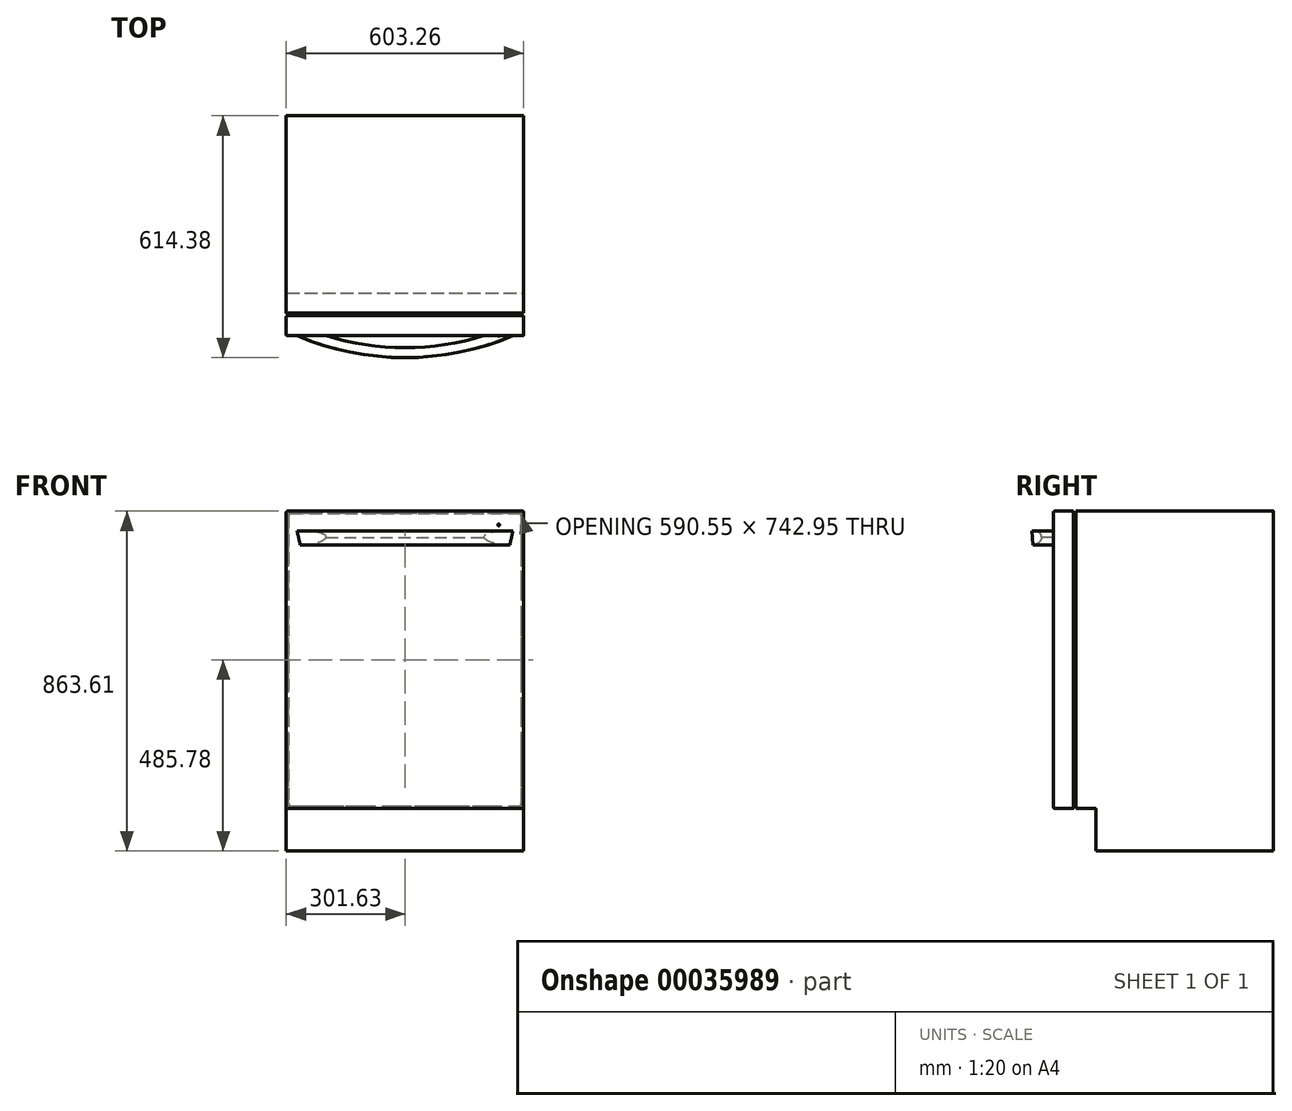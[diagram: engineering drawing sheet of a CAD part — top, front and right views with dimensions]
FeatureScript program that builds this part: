
annotation { "Feature Type Name" : "Feature", "Feature Type Description" : "" }
export const myFeature = defineFeature(function(context is Context, id is Id, definition is map)
    precondition{}
    {
        {
            var Q0;
            Q0=qCreatedBy(makeId("Front.planeOp"),FACE);
            var sketch = newSketch(context, id + "F0", { "sketchPlane" : qUnion([Q0])});
            skLineSegment(sketch, "E0.bottom", {"start": v(-301.63, 377.83) * mm, "end": v(301.63, 377.83) * mm});
            skLineSegment(sketch, "E0.top", {"start": v(-301.63, -377.82) * mm, "end": v(301.63, -377.82) * mm});
            skLineSegment(sketch, "E0.left", {"start": v(-301.63, 377.83) * mm, "end": v(-301.63, -377.82) * mm});
            skLineSegment(sketch, "E0.right", {"start": v(301.63, 377.83) * mm, "end": v(301.63, -377.82) * mm});
            skLineSegment(sketch, "E1", {"start": v(-301.63, -377.83) * mm, "end": v(301.63, 377.83) * mm, "construction": true});
            skPoint(sketch, "E2", {"position": v(0, 0) * mm});
            skSolve(sketch);
        }
        {
            var Q0;
            Q0=makeQuery(id+"F0.imprint","IMPRINT",FACE,{"disambiguationData":[TD([[makeQuery(id+"F0.imprint","IMPRINT",EDGE,{"derivedFrom":sQuery(id+"F0.wireOp",EDGE,"E0.bottom")}),-1.0]])]});
            extrude(context, id + "F1", {"entities" : qUnion([Q0]), "depth" : 50.8 * mm});
        }
        {
            var Q0;
            Q0=makeQuery(id+"F1.opExtrude","CAP_FACE",FACE,{"disambiguationData":[OSD([sQuery(id+"F0.wireOp",EDGE,"E0.bottom"),sQuery(id+"F0.wireOp",EDGE,"E0.top"),sQuery(id+"F0.wireOp",EDGE,"E0.left"),sQuery(id+"F0.wireOp",EDGE,"E0.right")])],"isStart":true});
            var sketch = newSketch(context, id + "F2", { "sketchPlane" : qUnion([Q0])});
            skLineSegment(sketch, "E3.0", {"start": v(295.28, 371.48) * mm, "end": v(295.28, -371.47) * mm});
            skLineSegment(sketch, "E3.1", {"start": v(295.28, 371.48) * mm, "end": v(-295.28, 371.48) * mm});
            skLineSegment(sketch, "E3.2", {"start": v(-295.28, 371.48) * mm, "end": v(-295.28, -371.47) * mm});
            skLineSegment(sketch, "E3.3", {"start": v(295.28, -371.47) * mm, "end": v(-295.28, -371.47) * mm});
            skSolve(sketch);
        }
        {
            var Q0;
            Q0=makeQuery(id+"F2.imprint","IMPRINT",FACE,{"disambiguationData":[TD([[makeQuery(id+"F2.imprint","IMPRINT",EDGE,{"derivedFrom":sQuery(id+"F2.wireOp",EDGE,"E3.0")}),-1.0]])]});
            extrude(context, id + "F3", {"entities" : qUnion([Q0]), "operationType" : NewBodyOperationType.ADD, "depth" : 6.35 * mm});
        }
        {
            var Q0;
            Q0=makeQuery(id+"F3.opExtrude","CAP_FACE",FACE,{"disambiguationData":[OSD([sQuery(id+"F2.wireOp",EDGE,"E3.0"),sQuery(id+"F2.wireOp",EDGE,"E3.1"),sQuery(id+"F2.wireOp",EDGE,"E3.2"),sQuery(id+"F2.wireOp",EDGE,"E3.3")])],"isStart":false});
            var sketch = newSketch(context, id + "F4", { "sketchPlane" : qUnion([Q0])});
            skLineSegment(sketch, "E4.bottom", {"start": v(301.63, 377.83) * mm, "end": v(-301.63, 377.82) * mm});
            skLineSegment(sketch, "E4.top", {"start": v(301.63, -485.77) * mm, "end": v(-301.62, -485.77) * mm});
            skLineSegment(sketch, "E4.left", {"start": v(301.63, 377.83) * mm, "end": v(301.63, -485.77) * mm});
            skLineSegment(sketch, "E4.right", {"start": v(-301.63, 377.82) * mm, "end": v(-301.62, -485.77) * mm});
            skSolve(sketch);
        }
        {
            var Q0;
            Q0=makeQuery(id+"F4.imprint","IMPRINT",FACE,{"disambiguationData":[TD([[makeQuery(id+"F4.imprint","IMPRINT",EDGE,{"derivedFrom":makeQuery(id+"F3.opExtrude","CAP_EDGE",EDGE,{"disambiguationData":[OSD([sQuery(id+"F2.wireOp",EDGE,"E3.0")])],"isStart":false})}),-1.0]])]});
            var Q1;
            Q1=makeQuery(id+"F4.imprint","IMPRINT",FACE,{"disambiguationData":[TD([[makeQuery(id+"F4.imprint","IMPRINT",EDGE,{"derivedFrom":sQuery(id+"F4.wireOp",EDGE,"E4.bottom")}),1.0]])]});
            extrude(context, id + "F5", {"entities" : qUnion([Q0, Q1]), "operationType" : NewBodyOperationType.ADD, "depth" : 501.65 * mm});
        }
        {
            var Q0;
            Q0=makeQuery(id+"F5.opExtrude","SWEPT_FACE",FACE,{"disambiguationData":[OSD([sQuery(id+"F4.wireOp",EDGE,"E4.right")])]});
            var sketch = newSketch(context, id + "F6", { "sketchPlane" : qUnion([Q0])});
            skLineSegment(sketch, "E5.bottom", {"start": v(-50.8, -377.82) * mm, "end": v(57.15, -377.82) * mm});
            skLineSegment(sketch, "E5.top", {"start": v(-50.8, -485.77) * mm, "end": v(57.15, -485.77) * mm});
            skLineSegment(sketch, "E5.left", {"start": v(-50.8, -377.82) * mm, "end": v(-50.8, -485.77) * mm});
            skLineSegment(sketch, "E5.right", {"start": v(57.15, -377.82) * mm, "end": v(57.15, -485.77) * mm});
            skSolve(sketch);
        }
        {
            var Q0;
            {var subQ6=sQuery(id+"F6.wireOp",EDGE,"E5.right");Q0=makeQuery(id+"F6.imprint","IMPRINT",FACE,{"disambiguationData":[TD([[makeQuery(id+"F6.imprint","IMPRINT",EDGE,{"derivedFrom":subQ6}),-1.0]])]});}
            extrude(context, id + "F7", {"entities" : qUnion([Q0]), "operationType" : NewBodyOperationType.REMOVE, "endBound" : BoundingType.THROUGH_ALL, "oppositeDirection" : true, "depth" : 25.4 * mm});
        }
        {
            var Q0;
            Q0=makeQuery(id+"F5.opExtrude","SWEPT_EDGE",EDGE,{"disambiguationData":[OSD([sQuery(id+"F4.wireOp",EDGE,"E4.bottom"),sQuery(id+"F4.wireOp",EDGE,"E4.right")])]});
            var Q1;
            Q1=makeQuery(id+"F1.opExtrude","SWEPT_EDGE",EDGE,{"disambiguationData":[OSD([sQuery(id+"F0.wireOp",EDGE,"E0.bottom"),sQuery(id+"F0.wireOp",EDGE,"E0.right")])]});
            var Q2;
            Q2=makeQuery(id+"F5.opExtrude","SWEPT_EDGE",EDGE,{"disambiguationData":[OSD([sQuery(id+"F4.wireOp",EDGE,"E4.bottom"),sQuery(id+"F4.wireOp",EDGE,"E4.left")])]});
            var Q3;
            Q3=makeQuery(id+"F1.opExtrude","SWEPT_FACE",FACE,{"disambiguationData":[OSD([sQuery(id+"F0.wireOp",EDGE,"E0.bottom")])]});
            var Q4;
            Q4=makeQuery(id+"F1.opExtrude","CAP_FACE",FACE,{"disambiguationData":[OSD([sQuery(id+"F0.wireOp",EDGE,"E0.bottom"),sQuery(id+"F0.wireOp",EDGE,"E0.top"),sQuery(id+"F0.wireOp",EDGE,"E0.left"),sQuery(id+"F0.wireOp",EDGE,"E0.right")])],"isStart":false});
            var Q5;
            Q5=makeQuery(id+"F1.opExtrude","SWEPT_FACE",FACE,{"disambiguationData":[OSD([sQuery(id+"F0.wireOp",EDGE,"E0.left")])]});
            var Q6;
            Q6=makeQuery(id+"F1.opExtrude","SWEPT_FACE",FACE,{"disambiguationData":[OSD([sQuery(id+"F0.wireOp",EDGE,"E0.top")])]});
            var Q7;
            Q7=makeQuery(id+"F1.opExtrude","SWEPT_FACE",FACE,{"disambiguationData":[OSD([sQuery(id+"F0.wireOp",EDGE,"E0.right")])]});
            var Q8;
            Q8=makeQuery(id+"F7.boolean.opBoolean","COPY",EDGE,{"derivedFrom":makeQuery(id+"F7.opExtrude","CAP_EDGE",EDGE,{"disambiguationData":[OSD([sQuery(id+"F6.wireOp",EDGE,"E5.bottom")])],"isStart":true})});
            var Q9;
            Q9=makeQuery(id+"F7.boolean.opBoolean","INTERSECT",EDGE,{"derivedFrom":[makeQuery(id+"F5.opExtrude","SWEPT_FACE",FACE,{"disambiguationData":[OSD([sQuery(id+"F4.wireOp",EDGE,"E4.left")])]}),makeQuery(id+"F7.opExtrude","SWEPT_FACE",FACE,{"disambiguationData":[OSD([sQuery(id+"F6.wireOp",EDGE,"E5.bottom")])]})]});
            fillet(context, id + "F8", {"entities" : qUnion([Q0, Q1, Q2, Q3, Q4, Q5, Q6, Q7, Q8, Q9]), "radius" : 3.17 * mm, "tangentPropagation" : true, "rho" : 0.5, "crossSection" : FilletCrossSection.CONIC, "allowEdgeOverflow" : false});
        }
        {
            var Q0;
            Q0=makeQuery(id+"F3.opExtrude","SWEPT_EDGE",EDGE,{"disambiguationData":[OSD([sQuery(id+"F2.wireOp",EDGE,"E3.1"),sQuery(id+"F2.wireOp",EDGE,"E3.2")])]});
            var Q1;
            Q1=makeQuery(id+"F3.opExtrude","SWEPT_EDGE",EDGE,{"disambiguationData":[OSD([sQuery(id+"F2.wireOp",EDGE,"E3.0"),sQuery(id+"F2.wireOp",EDGE,"E3.1")])]});
            var Q2;
            Q2=makeQuery(id+"F3.opExtrude","SWEPT_EDGE",EDGE,{"disambiguationData":[OSD([sQuery(id+"F2.wireOp",EDGE,"E3.0"),sQuery(id+"F2.wireOp",EDGE,"E3.3")])]});
            var Q3;
            Q3=makeQuery(id+"F3.opExtrude","SWEPT_EDGE",EDGE,{"disambiguationData":[OSD([sQuery(id+"F2.wireOp",EDGE,"E3.2"),sQuery(id+"F2.wireOp",EDGE,"E3.3")])]});
            fillet(context, id + "F9", {"entities" : qUnion([Q0, Q1, Q2, Q3]), "radius" : 6.35 * mm, "tangentPropagation" : true, "allowEdgeOverflow" : false});
        }
        {
            var Q0;
            Q0=makeQuery(id+"F1.opExtrude","SWEPT_FACE",FACE,{"disambiguationData":[OSD([sQuery(id+"F0.wireOp",EDGE,"E0.bottom")])]});
            cPlane(context, id + "F10", {"entities" : qUnion([Q0]), "cplaneType" : CPlaneType.OFFSET, "offset" : 50.8 * mm, "oppositeDirection" : true, "width" : 152.4 * mm, "height" : 152.4 * mm});
        }
        {
            var Q0;
            Q0=qCreatedBy(id+"F10.planeOp",FACE);
            var sketch = newSketch(context, id + "F11", { "sketchPlane" : qUnion([Q0])});
            skArc(sketch, "E6", {"start": v(-292.1, -42.88) * mm, "mid": v(0, -106.38) * mm, "end": v(292.1, -42.88) * mm});
            skLineSegment(sketch, "E7", {"start": v(-292.1, -106.38) * mm, "end": v(292.1, -106.38) * mm, "construction": true});
            skLineSegment(sketch, "E8", {"start": v(292.1, -106.38) * mm, "end": v(292.1, -42.88) * mm, "construction": true});
            skLineSegment(sketch, "E9", {"start": v(-292.1, -106.38) * mm, "end": v(-292.1, -42.88) * mm, "construction": true});
            skPoint(sketch, "E10", {"position": v(0, -106.38) * mm});
            skLineSegment(sketch, "E11", {"start": v(-292.1, -42.88) * mm, "end": v(292.1, -42.88) * mm, "construction": true});
            skSolve(sketch);
        }
        {
            var Q0;
            Q0=sQuery(id+"F11.wireOp",VERTEX,"E11.start");
            var Q1;
            Q1=sQuery(id+"F11.wireOp",EDGE,"E6");
            cPlane(context, id + "F12", {"entities" : qUnion([Q0, Q1]), "cplaneType" : CPlaneType.CURVE_POINT, "offset" : 152.4 * mm, "width" : 152.4 * mm, "height" : 152.4 * mm});
        }
        {
            var Q0;
            Q0=qCreatedBy(id+"F12.planeOp",FACE);
            var sketch = newSketch(context, id + "F13", { "sketchPlane" : qUnion([Q0])});
            skLineSegment(sketch, "E12.bottom", {"start": v(-160.27, 327.03) * mm, "end": v(-134.87, 327.03) * mm, "construction": true});
            skLineSegment(sketch, "E12.top", {"start": v(-160.27, 292.1) * mm, "end": v(-134.87, 292.1) * mm, "construction": true});
            skLineSegment(sketch, "E12.left", {"start": v(-160.27, 327.03) * mm, "end": v(-160.27, 292.1) * mm, "construction": true});
            skLineSegment(sketch, "E12.right", {"start": v(-134.87, 327.03) * mm, "end": v(-134.87, 292.1) * mm, "construction": true});
            skLineSegment(sketch, "E13", {"start": v(-160.27, 327.03) * mm, "end": v(-157.22, 292.1) * mm});
            skArc(sketch, "E14", {"start": v(-157.22, 292.1) * mm, "mid": v(-142.51, 297.53) * mm, "end": v(-134.87, 311.23) * mm});
            skArc(sketch, "E15", {"start": v(-134.87, 311.23) * mm, "mid": v(-139.5, 322.4) * mm, "end": v(-150.67, 327.03) * mm});
            skLineSegment(sketch, "E16", {"start": v(-150.67, 327.03) * mm, "end": v(-160.27, 327.03) * mm});
            skSolve(sketch);
        }
        {
            var Q0;
            Q0=makeQuery(id+"F13.imprint","IMPRINT",FACE,{"disambiguationData":[TD([[makeQuery(id+"F13.imprint","IMPRINT",EDGE,{"derivedFrom":sQuery(id+"F13.wireOp",EDGE,"E13")}),1.0]])]});
            var Q1;
            Q1=sQuery(id+"F11.wireOp",EDGE,"E6");
            sweep(context, id + "F14", {"operationType" : NewBodyOperationType.ADD, "profiles" : qUnion([Q0]), "path" : qUnion([Q1])});
        }
        {
            var Q0;
            Q0=makeQuery(id+"F5.opExtrude","SWEPT_FACE",FACE,{"disambiguationData":[OSD([sQuery(id+"F4.wireOp",EDGE,"E4.bottom")])]});
            cPlane(context, id + "F15", {"entities" : qUnion([Q0]), "cplaneType" : CPlaneType.OFFSET, "offset" : 34.92 * mm, "oppositeDirection" : true, "width" : 152.4 * mm, "height" : 152.4 * mm});
        }
        {
            var Q0;
            Q0=qCreatedBy(id+"F15.planeOp",FACE);
            var sketch = newSketch(context, id + "F16", { "sketchPlane" : qUnion([Q0])});
            skFitSpline(sketch, "E17.0", {"points": [v(298.45, -50.8) * mm, v(99.48, -50.8) * mm, v(-99.48, -50.8) * mm, v(-298.45, -50.8) * mm], "construction": true});
            skFitSpline(sketch, "E18.0", {"points": [v(301.63, -3.18) * mm, v(301.63, -18) * mm, v(301.63, -32.8) * mm, v(301.63, -47.62) * mm], "construction": true});
            skArc(sketch, "E19", {"start": v(238.13, -51.59) * mm, "mid": v(239.38, -51.39) * mm, "end": v(240.5, -50.8) * mm});
            skLineSegment(sketch, "E20", {"start": v(238.13, -50) * mm, "end": v(240.5, -50) * mm});
            skLineSegment(sketch, "E21", {"start": v(238.13, -51.59) * mm, "end": v(238.13, -50) * mm});
            skLineSegment(sketch, "E22", {"start": v(240.5, -50.8) * mm, "end": v(240.5, -50) * mm});
            skLineSegment(sketch, "E23", {"start": v(238.13, -51.59) * mm, "end": v(240.5, -51.59) * mm, "construction": true});
            skSolve(sketch);
        }
        {
            var Q0;
            Q0=makeQuery(id+"F16.imprint","IMPRINT",FACE,{"disambiguationData":[TD([[makeQuery(id+"F16.imprint","IMPRINT",EDGE,{"derivedFrom":sQuery(id+"F16.wireOp",EDGE,"E19")}),1.0]])]});
            var Q1;
            Q1=sQuery(id+"F16.wireOp",EDGE,"E21");
            revolve(context, id + "F17", {"operationType" : NewBodyOperationType.ADD, "entities" : qUnion([Q0]), "axis" : qUnion([Q1]), "revolveType" : RevolveType.FULL});
        }
    });
